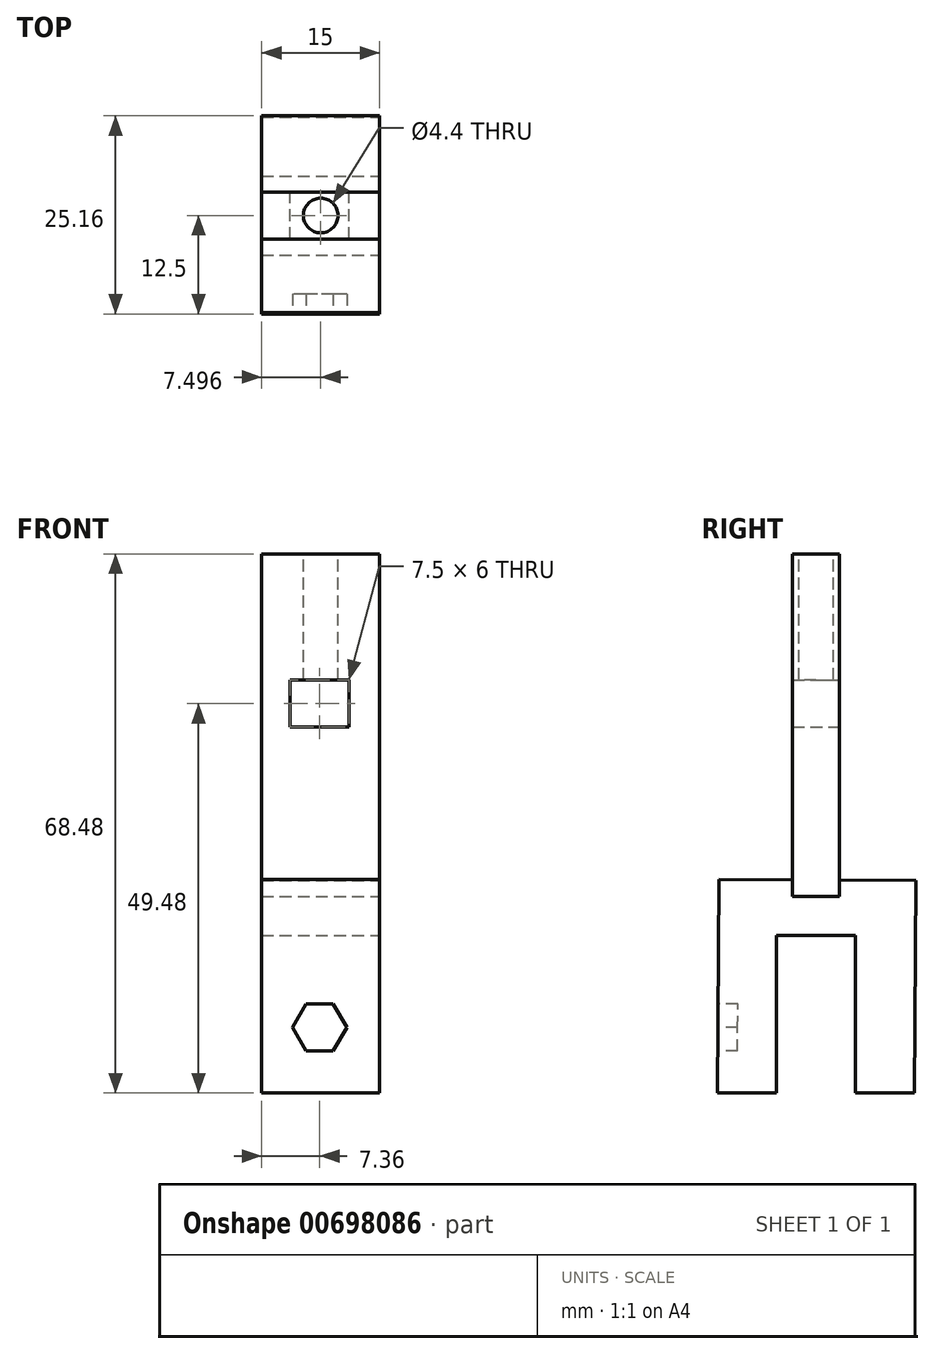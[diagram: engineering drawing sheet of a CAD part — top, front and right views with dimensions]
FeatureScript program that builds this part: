
annotation { "Feature Type Name" : "Feature", "Feature Type Description" : "" }
export const myFeature = defineFeature(function(context is Context, id is Id, definition is map)
    precondition{}
    {
        {
            var Q0;
            Q0=qCreatedBy(makeId("Front.planeOp"),FACE);
            var sketch = newSketch(context, id + "F0", { "sketchPlane" : qUnion([Q0])});
            skLineSegment(sketch, "E0.bottom", {"start": v(-7.36, 71.48) * mm, "end": v(7.64, 71.48) * mm});
            skLineSegment(sketch, "E0.left", {"start": v(-7.36, 71.48) * mm, "end": v(-7.36, 0) * mm});
            skLineSegment(sketch, "E0.right", {"start": v(7.64, 71.48) * mm, "end": v(7.64, 0) * mm});
            skLineSegment(sketch, "E1.bottom", {"start": v(3.75, 55.48) * mm, "end": v(-3.75, 55.48) * mm});
            skLineSegment(sketch, "E1.top", {"start": v(3.75, 49.48) * mm, "end": v(-3.75, 49.48) * mm});
            skLineSegment(sketch, "E1.left", {"start": v(3.75, 55.48) * mm, "end": v(3.75, 49.48) * mm});
            skLineSegment(sketch, "E1.right", {"start": v(-3.75, 55.48) * mm, "end": v(-3.75, 49.48) * mm});
            skPoint(sketch, "E1.middle", {"position": v(0, 52.48) * mm});
            skPoint(sketch, "E2.middle", {"position": v(0, 62.48) * mm});
            skLineSegment(sketch, "E3", {"start": v(0, 0) * mm, "end": v(0, 49.48) * mm, "construction": true});
            skLineSegment(sketch, "E4", {"start": v(0, 59.48) * mm, "end": v(0, 55.48) * mm, "construction": true});
            skLineSegment(sketch, "E5", {"start": v(0, 71.48) * mm, "end": v(0, 65.48) * mm, "construction": true});
            skLineSegment(sketch, "E6", {"start": v(7.64, 28) * mm, "end": v(-7.36, 28) * mm});
            skSolve(sketch);
        }
        {
            var Q0;
            Q0=makeQuery(id+"F0.imprint","IMPRINT",FACE,{"disambiguationData":[TD([[makeQuery(id+"F0.imprint","IMPRINT",EDGE,{"derivedFrom":sQuery(id+"F0.wireOp",EDGE,"E0.bottom")}),-1.0]])]});
            extrude(context, id + "F1", {"entities" : qUnion([Q0]), "depth" : 6 * mm, "offsetDistance" : 25 * mm});
        }
        {
            var Q0;
            Q0=makeQuery(id+"F1.opExtrude","SWEPT_FACE",FACE,{"disambiguationData":[OSD([sQuery(id+"F0.wireOp",EDGE,"E0.right")])]});
            var sketch = newSketch(context, id + "F2", { "sketchPlane" : qUnion([Q0])});
            skLineSegment(sketch, "E7", {"start": v(-3, 3) * mm, "end": v(-3, 30) * mm, "construction": true});
            skLineSegment(sketch, "E8.bottom", {"start": v(9.66, 30) * mm, "end": v(-15.34, 30.15) * mm});
            skLineSegment(sketch, "E8.top", {"start": v(9.5, 3) * mm, "end": v(-15.5, 3) * mm});
            skLineSegment(sketch, "E8.left", {"start": v(9.66, 30) * mm, "end": v(9.5, 3) * mm});
            skLineSegment(sketch, "E8.right", {"start": v(-15.34, 30.15) * mm, "end": v(-15.5, 3) * mm});
            skLineSegment(sketch, "E9", {"start": v(-6, 30) * mm, "end": v(0, 30) * mm, "construction": true});
            skPoint(sketch, "E10", {"position": v(-3, 30) * mm});
            skPoint(sketch, "E11", {"position": v(-3, 38.59) * mm});
            skLineSegment(sketch, "E12.bottom", {"start": v(-8, 23) * mm, "end": v(2, 23) * mm});
            skLineSegment(sketch, "E12.top", {"start": v(-8, 3) * mm, "end": v(2, 3) * mm});
            skLineSegment(sketch, "E12.left", {"start": v(-8, 23) * mm, "end": v(-8, 3) * mm});
            skLineSegment(sketch, "E12.right", {"start": v(2, 23) * mm, "end": v(2, 3) * mm});
            skPoint(sketch, "E12.middle", {"position": v(-3, 13) * mm});
            skSolve(sketch);
        }
        {
            var Q0;
            {var subQ8=sQuery(id+"F2.wireOp",EDGE,"E8.right");Q0=makeQuery(id+"F2.imprint","IMPRINT",FACE,{"disambiguationData":[TD([[makeQuery(id+"F2.imprint","IMPRINT",EDGE,{"derivedFrom":subQ8}),1.0]])]});}
            extrude(context, id + "F3", {"entities" : qUnion([Q0]), "oppositeDirection" : true, "depth" : 15 * mm, "hasOffset" : true, "offsetDistance" : 25 * mm});
        }
        {
            var Q0;
            Q0=makeQuery(id+"F1.opExtrude","SWEPT_FACE",FACE,{"disambiguationData":[OSD([sQuery(id+"F0.wireOp",EDGE,"E0.bottom")])]});
            var sketch = newSketch(context, id + "F4", { "sketchPlane" : qUnion([Q0])});
            skPoint(sketch, "E13", {"position": v(0.14, -3) * mm});
            skPoint(sketch, "E13.positionSnap0", {"position": v(7.64, -3) * mm});
            skPoint(sketch, "E13.positionSnap1", {"position": v(0.14, -6) * mm});
            skCircle(sketch, "E14", {"center": v(0.14, -3) * mm, "radius": 1.6 * mm});
            skSolve(sketch);
        }
        {
            var Q0;
            Q0=sQuery(id+"F4.wireOp",VERTEX,"E13");
            var Q1;
            Q1=makeQuery(id+"F1.opExtrude","SWEPT_BODY",BODY,{"disambiguationData":[OSD([sQuery(id+"F0.wireOp",EDGE,"E0.bottom"),sQuery(id+"F0.wireOp",EDGE,"E0.left"),sQuery(id+"F0.wireOp",EDGE,"E0.right"),sQuery(id+"F0.wireOp",EDGE,"E1.bottom"),sQuery(id+"F0.wireOp",EDGE,"E1.top"),sQuery(id+"F0.wireOp",EDGE,"E1.left"),sQuery(id+"F0.wireOp",EDGE,"E1.right"),sQuery(id+"F0.wireOp",EDGE,"E2.bottom"),sQuery(id+"F0.wireOp",EDGE,"E2.top"),sQuery(id+"F0.wireOp",EDGE,"E2.left"),sQuery(id+"F0.wireOp",EDGE,"E2.right"),sQuery(id+"F0.wireOp",EDGE,"E6")])]});
            hole(context, id + "F5", {"style" : HoleStyle.SIMPLE, "endStyle" : HoleEndStyle.BLIND, "standardTappedOrClearance" : lookupTablePath({ "standard" : "ISO", "fit" : "Normal", "size" : "M4", "type" : "Clearance" }), "standardBlindInLast" : lookupTablePath({ "fit" : "Standard", "standard" : "ISO", "size" : "M4", "type" : "Clearance" }), "holeDiameter" : 4.4 * mm, "majorDiameter" : 5 * mm, "holeDepth" : 20 * mm, "isTappedThrough" : true, "tappedDepth" : 12 * mm, "tapClearance" : 3, "locations" : qUnion([Q0]), "scope" : qUnion([Q1])});
        }
        {
            var Q0;
            Q0=makeQuery(id+"F3.opExtrude","SWEPT_FACE",FACE,{"disambiguationData":[OSD([sQuery(id+"F2.wireOp",EDGE,"E8.right")])]});
            var sketch = newSketch(context, id + "F6", { "sketchPlane" : qUnion([Q0])});
            skLineSegment(sketch, "E15", {"start": v(-7.36, 19.9) * mm, "end": v(7.64, 19.9) * mm, "construction": true});
            skLineSegment(sketch, "E16", {"start": v(7.64, 19.9) * mm, "end": v(-7.36, 2.9) * mm, "construction": true});
            skPoint(sketch, "E17", {"position": v(0, 11.26) * mm});
            skCircle(sketch, "E18.cCircle", {"center": v(0, 11.26) * mm, "radius": 3 * mm, "construction": true});
            skLineSegment(sketch, "E18.0", {"start": v(-1.73, 14.26) * mm, "end": v(1.73, 14.26) * mm});
            skLineSegment(sketch, "E18.1", {"start": v(1.73, 14.26) * mm, "end": v(3.46, 11.26) * mm});
            skLineSegment(sketch, "E18.2", {"start": v(3.46, 11.26) * mm, "end": v(1.73, 8.26) * mm});
            skLineSegment(sketch, "E18.3", {"start": v(1.73, 8.26) * mm, "end": v(-1.73, 8.26) * mm});
            skLineSegment(sketch, "E18.4", {"start": v(-1.73, 8.26) * mm, "end": v(-3.46, 11.26) * mm});
            skLineSegment(sketch, "E18.5", {"start": v(-3.46, 11.26) * mm, "end": v(-1.73, 14.26) * mm});
            skPoint(sketch, "E18.0.midPoint", {"position": v(0, 14.26) * mm});
            skSolve(sketch);
        }
        {
            var Q0;
            Q0=sQuery(id+"F6.wireOp",VERTEX,"E17");
            var Q1;
            Q1=makeQuery(id+"F1.opExtrude","SWEPT_BODY",BODY,{"disambiguationData":[OSD([sQuery(id+"F0.wireOp",EDGE,"E0.bottom"),sQuery(id+"F0.wireOp",EDGE,"E0.left"),sQuery(id+"F0.wireOp",EDGE,"E0.right"),sQuery(id+"F0.wireOp",EDGE,"E1.bottom"),sQuery(id+"F0.wireOp",EDGE,"E1.top"),sQuery(id+"F0.wireOp",EDGE,"E1.left"),sQuery(id+"F0.wireOp",EDGE,"E1.right"),sQuery(id+"F0.wireOp",EDGE,"E2.bottom"),sQuery(id+"F0.wireOp",EDGE,"E2.top"),sQuery(id+"F0.wireOp",EDGE,"E2.left"),sQuery(id+"F0.wireOp",EDGE,"E2.right"),sQuery(id+"F0.wireOp",EDGE,"E6")])]});
            hole(context, id + "F7", {"style" : HoleStyle.SIMPLE, "endStyle" : HoleEndStyle.BLIND, "standardTappedOrClearance" : lookupTablePath({ "standard" : "ISO", "fit" : "Normal", "size" : "M3", "type" : "Clearance" }), "standardBlindInLast" : lookupTablePath({ "fit" : "Standard", "standard" : "ISO", "size" : "M3", "type" : "Clearance" }), "holeDiameter" : 3.3 * mm, "majorDiameter" : 5 * mm, "holeDepth" : 40 * mm, "isTappedThrough" : true, "tappedDepth" : 12 * mm, "tapClearance" : 3, "locations" : qUnion([Q0]), "scope" : qUnion([Q1])});
        }
        {
            var Q0;
            Q0=makeQuery(id+"F6.imprint","IMPRINT",FACE,{"disambiguationData":[TD([[makeQuery(id+"F6.imprint","IMPRINT",EDGE,{"derivedFrom":sQuery(id+"F6.wireOp",EDGE,"E18.0")}),-1.0]])]});
            extrude(context, id + "F8", {"entities" : qUnion([Q0]), "operationType" : NewBodyOperationType.REMOVE, "oppositeDirection" : true, "depth" : 2.5 * mm, "offsetDistance" : 25 * mm});
        }
    });
